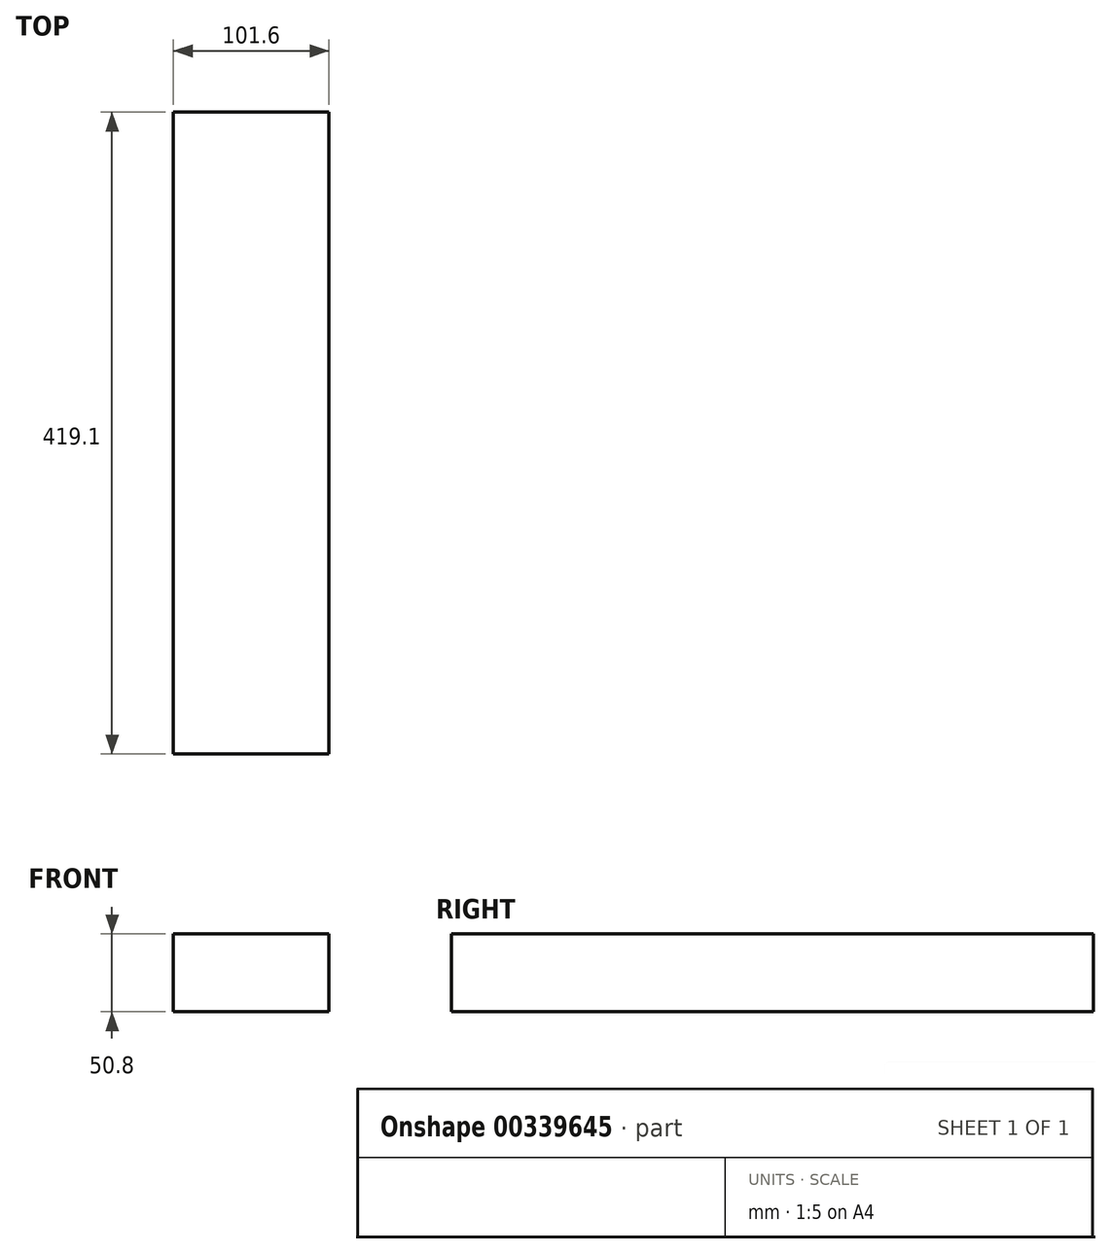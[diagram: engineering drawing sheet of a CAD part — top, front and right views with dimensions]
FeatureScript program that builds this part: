
annotation { "Feature Type Name" : "Feature", "Feature Type Description" : "" }
export const myFeature = defineFeature(function(context is Context, id is Id, definition is map)
    precondition{}
    {
        {
            var Q0;
            Q0=qCreatedBy(makeId("Front.planeOp"),FACE);
            var sketch = newSketch(context, id + "F0", { "sketchPlane" : qUnion([Q0])});
            skLineSegment(sketch, "E0.bottom", {"start": v(0, 0) * mm, "end": v(101.6, 0) * mm});
            skLineSegment(sketch, "E0.top", {"start": v(0, 50.8) * mm, "end": v(101.6, 50.8) * mm});
            skLineSegment(sketch, "E0.left", {"start": v(0, 0) * mm, "end": v(0, 50.8) * mm});
            skLineSegment(sketch, "E0.right", {"start": v(101.6, 0) * mm, "end": v(101.6, 50.8) * mm});
            skSolve(sketch);
        }
        {
            var Q0;
            Q0=makeQuery(id+"F0.imprint","IMPRINT",FACE,{"disambiguationData":[TD([[makeQuery(id+"F0.imprint","IMPRINT",EDGE,{"derivedFrom":sQuery(id+"F0.wireOp",EDGE,"E0.bottom")}),1.0]])]});
            extrude(context, id + "F1", {"entities" : qUnion([Q0]), "depth" : 419.1 * mm});
        }
    });
